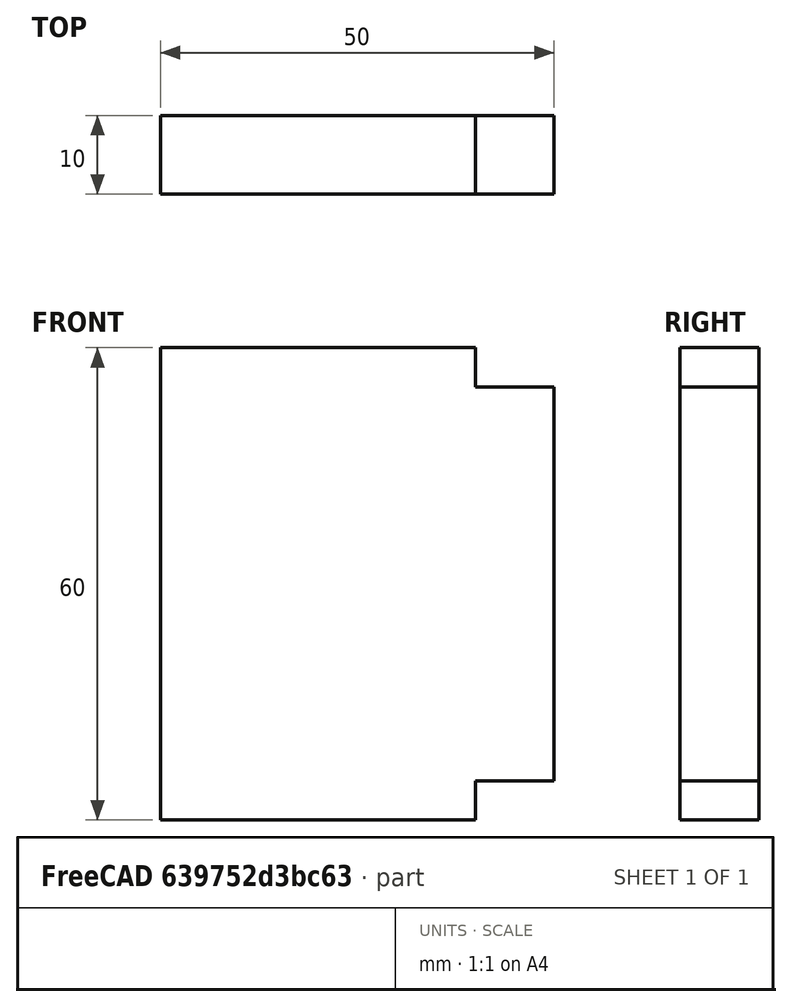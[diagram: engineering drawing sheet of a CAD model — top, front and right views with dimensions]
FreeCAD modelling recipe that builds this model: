
FCSTD DOCUMENT  (FreeCAD 0.16R)
Label: fixation_panneau_avant
License: All rights reserved
LicenseURL: http://fr.wikipedia.org/wiki/<copyright redacted>
objects: Sketcher::SketchObject×1, PartDesign::Pad×1
note: 3 computed .brp shape members not serialized (recipe doc carries the construction recipe); baked Part::Feature solids carry a one-line shape summary decoded from their .brp

FEATURE [Sketcher::SketchObject] Sketch
  Placement = pos=(0,0,0) rot=(-1,0,0;4.71239rad)
  sketch-geometry (8):
    g0: LineSegment StartX=0 StartY=0 StartZ=0 EndX=0 EndY=60 EndZ=0
    g1: LineSegment StartX=0 StartY=60 StartZ=0 EndX=40 EndY=60 EndZ=0
    g2: LineSegment StartX=40 StartY=60 StartZ=0 EndX=40 EndY=55 EndZ=0
    g3: LineSegment StartX=40 StartY=55 StartZ=0 EndX=50 EndY=55 EndZ=0
    g4: LineSegment StartX=50 StartY=55 StartZ=0 EndX=50 EndY=5 EndZ=0
    g5: LineSegment StartX=50 StartY=5 StartZ=0 EndX=40 EndY=5 EndZ=0
    g6: LineSegment StartX=40 StartY=5 StartZ=0 EndX=40 EndY=0 EndZ=0
    g7: LineSegment StartX=40 StartY=0 StartZ=0 EndX=0 EndY=0 EndZ=0
  constraints (23):
    c: Coincident(g-1,g0)
    c: PointOnObject(g0,g-2)
    c: Coincident(g0,g1)
    c: Horizontal(g1)
    c: Coincident(g1,g2)
    c: Vertical(g2)
    c: Coincident(g2,g3)
    c: Coincident(g3,g4)
    c: Vertical(g4)
    c: Coincident(g4,g5)
    c: Horizontal(g5)
    c: Coincident(g5,g6)
    c: Vertical(g6)
    c: Coincident(g6,g7)
    c: Coincident(g7,g0)
    c: Horizontal(g7)
    c: Horizontal(g3)
    c: Equal(g2,g6)
    c: Equal(g5,g3)
    c: DistanceX(g5,g5) = 10
    c: DistanceY(g4,g4) = 50
    c: Distance(g0) = 60
    c: DistanceX(g-1,g4) = 50
FEATURE [PartDesign::Pad] Pad
  Length = 10
  Length2 = 100
  Placement = pos=(0,0,0) rot=(-1,0,0;4.71239rad)
  Sketch = -> Sketch
  Type = 0
